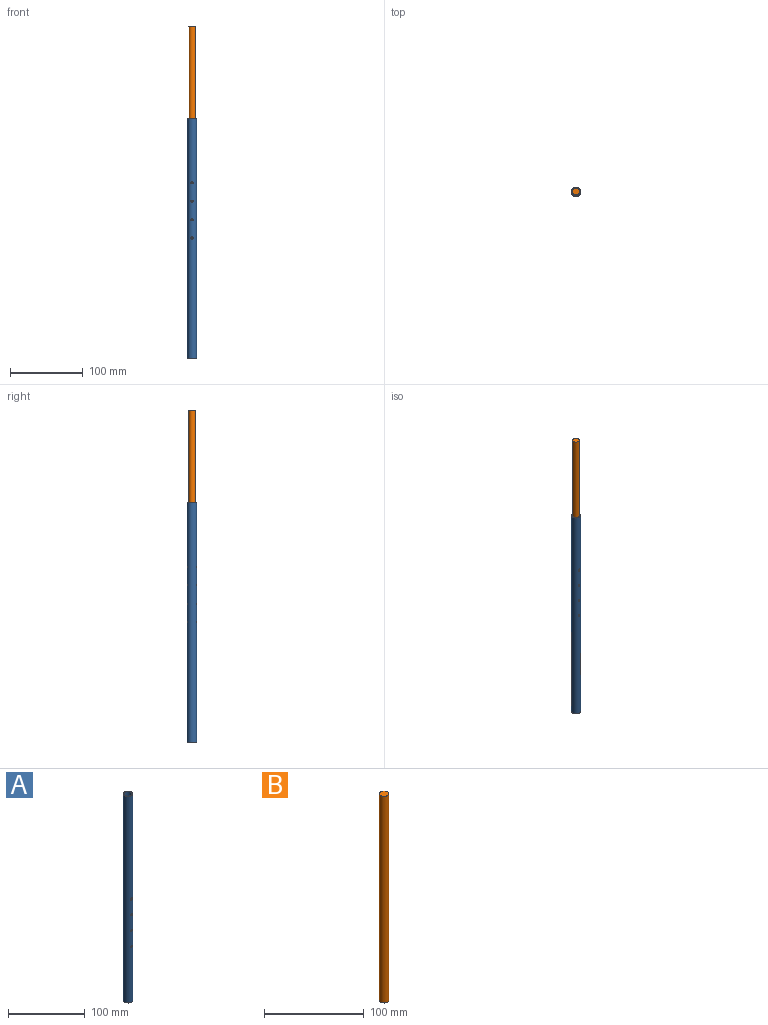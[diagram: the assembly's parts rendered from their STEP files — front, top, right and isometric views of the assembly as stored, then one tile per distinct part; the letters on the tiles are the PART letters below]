
ASSEMBLY  parts=2 mates=1
PART A: 12 faces, bbox 12.7x12.7x330.2 mm
  f0: cylinder r=6.35mm len=330.2mm, axis (0,0,-1), area 13110.4mm2, adj f2,f3,f4,f5,f6,f7,f8,f9
  f1: cylinder r=5.08mm len=330.2mm, axis (0,0,-1), area 10475.4mm2, adj f2,f3,f4,f5,f6,f7,f8,f9
  f2: plane 12.7x12.7mm, normal (0,0,1), area 45.6mm2, adj f0,f1
  f3: plane 12.7x12.7mm, normal (0,0,-1), area 45.6mm2, adj f0,f1
  f4: cylinder r=1.59mm len=3.18mm, axis (0,1,0), area 12.9mm2, adj f0,f1
  f5: cylinder r=1.59mm len=3.18mm, axis (0,1,0), area 12.9mm2, adj f0,f1
  f6: cylinder r=1.59mm len=3.18mm, axis (0,1,0), area 12.9mm2, adj f0,f1
  f7: cylinder r=1.59mm len=3.18mm, axis (0,1,0), area 12.9mm2, adj f0,f1
  f8: cylinder r=1.59mm len=3.18mm, axis (0,-1,0), area 12.9mm2, adj f0,f1
  f9: cylinder r=1.59mm len=3.18mm, axis (0,-1,0), area 12.9mm2, adj f0,f1
  f10: cylinder r=1.59mm len=3.18mm, axis (0,-1,0), area 12.9mm2, adj f0,f1
  f11: cylinder r=1.59mm len=3.18mm, axis (0,-1,0), area 12.9mm2, adj f0,f1
PART B: 3 faces, bbox 9.4x9.4x254 mm
  f0: cylinder r=4.7mm len=254mm, axis (0,0,-1), area 7499.3mm2, adj f1,f2
  f1: plane 9.4x9.4mm, normal (0,0,1), area 69.4mm2, adj f0
  f2: plane 9.4x9.4mm, normal (0,0,-1), area 69.4mm2, adj f0
PLACE A rot(axis=(0,1,0),180deg) t=(-199.88,-4.96,183.04)mm fixed
PLACE B t=(-199.88,-4.96,56.04)mm
MATE slider B.f0 <-> A.f1  axis (0,0,-1) through (-199.88,-4.96,183.04)mm
